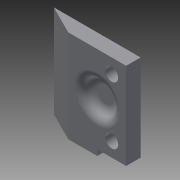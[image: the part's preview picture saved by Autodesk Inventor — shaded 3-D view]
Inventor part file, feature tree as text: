
AUTODESK INVENTOR PART (.ipt)
format: ipt  version: 2015 (Build 190159000, 159)  size: 125,952 bytes
history: native  units: in
note: dims shown in document units (in); Inventor stores cm internally (conversion verified against a paired STEP export)
features: extrude x4, sketch x2, plane x1, fillet x1
ambient origin geometry x8: Origin, YZ Plane, XZ Plane, XY Plane, X Axis, Y Axis, Z Axis, Center Point
bodies: Solid1 (feature_tree)
feature tree (8):
  sketch  "Sketch1"  dims[d13=0.0787in d15=0.3937in]
  extrude  "Extrusion2"  Depth=0.3937in
  plane  "Work Plane2"
  sketch  "Sketch2"  dims[d18=1.1811in d19=0.0in d20=0.3937in d21=0.3937in d22=0.5906in d23=0.1181in d24=0.0in d27=0.1181in d28=0.0787in d29=0.0in d30=0.1969in d31=0.1969in d32=0.1772in d33=0.3937in d34=0.1969in d35=0.1772in d36=0.7874in d37=0.0in]
  extrude  "Extrusion3"  Depth=0.3937in
  fillet  "Fillet3"  Radius=0.3937in
  extrude  "Extrusion4"  Depth=0.1969in
  extrude  "Extrusion5"  Depth=0.1181in TaperAngle=0.0deg
